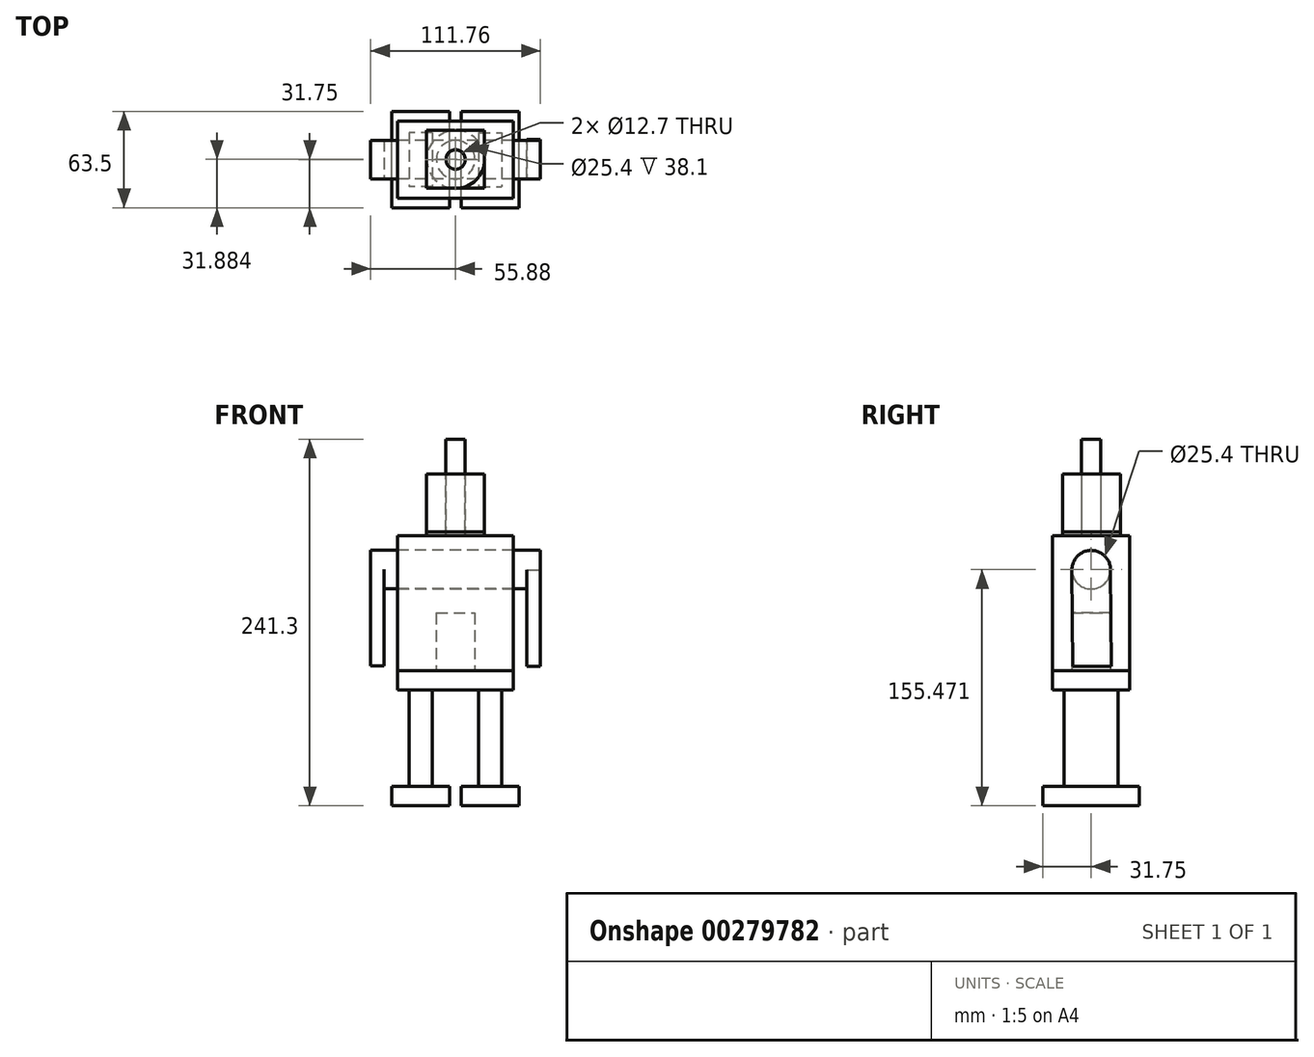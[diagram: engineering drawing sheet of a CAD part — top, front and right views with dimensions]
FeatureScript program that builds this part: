
annotation { "Feature Type Name" : "Feature", "Feature Type Description" : "" }
export const myFeature = defineFeature(function(context is Context, id is Id, definition is map)
    precondition{}
    {
        {
            var Q0;
            Q0=qCreatedBy(makeId("Front.planeOp"),FACE);
            var sketch = newSketch(context, id + "F0", { "sketchPlane" : qUnion([Q0])});
            skLineSegment(sketch, "E0.bottom", {"start": v(38.1, -57.15) * mm, "end": v(-38.1, -57.15) * mm});
            skLineSegment(sketch, "E0.top", {"start": v(38.1, 57.15) * mm, "end": v(-38.1, 57.15) * mm});
            skLineSegment(sketch, "E0.left", {"start": v(38.1, -57.15) * mm, "end": v(38.1, 57.15) * mm});
            skLineSegment(sketch, "E0.right", {"start": v(-38.1, -57.15) * mm, "end": v(-38.1, 57.15) * mm});
            skPoint(sketch, "E0.middle", {"position": v(0, 0) * mm});
            skSolve(sketch);
        }
        {
            var Q0;
            Q0 = qSketchRegion(id + "F0", true);
            extrude(context, id + "F1", {"entities" : qUnion([Q0]), "depth" : 50.8 * mm});
        }
        {
            var Q0;
            Q0=makeQuery(id+"F1.opExtrude","SWEPT_FACE",FACE,{"disambiguationData":[OSD([sQuery(id+"F0.wireOp",EDGE,"E0.left")])]});
            var sketch = newSketch(context, id + "F2", { "sketchPlane" : qUnion([Q0])});
            skCircle(sketch, "E1", {"center": v(-25.4, 34.82) * mm, "radius": 12.7 * mm});
            skPoint(sketch, "E1.centerSnap0", {"position": v(-25.4, 57.15) * mm});
            skSolve(sketch);
        }
        {
            var Q0;
            Q0 = qSketchRegion(id + "F2", true);
            extrude(context, id + "F3", {"entities" : qUnion([Q0]), "operationType" : NewBodyOperationType.REMOVE, "oppositeDirection" : true, "depth" : 76.2 * mm});
        }
        {
            var Q0;
            Q0=makeQuery(id+"F1.opExtrude","SWEPT_FACE",FACE,{"disambiguationData":[OSD([sQuery(id+"F0.wireOp",EDGE,"E0.bottom")])]});
            var sketch = newSketch(context, id + "F4", { "sketchPlane" : qUnion([Q0])});
            skCircle(sketch, "E2", {"center": v(0, 25.4) * mm, "radius": 12.7 * mm});
            skPoint(sketch, "E2.centerSnap0", {"position": v(-38.1, 25.4) * mm});
            skSolve(sketch);
        }
        {
            var Q0;
            Q0 = qSketchRegion(id + "F4", true);
            var Q1;
            Q1=makeQuery(id+"F4.imprint","IMPRINT",FACE,{"disambiguationData":[TD([[makeQuery(id+"F4.imprint","IMPRINT",EDGE,{"derivedFrom":sQuery(id+"F4.wireOp",EDGE,"E2")}),-1.0]])]});
            extrude(context, id + "F5", {"entities" : qUnion([Q0, Q1]), "operationType" : NewBodyOperationType.REMOVE, "oppositeDirection" : true, "depth" : 25.4 * mm});
        }
        {
            var Q0;
            Q0=makeQuery(id+"F5.boolean.opBoolean","COPY",FACE,{"derivedFrom":makeQuery(id+"F5.opExtrude","CAP_FACE",FACE,{"disambiguationData":[OSD([sQuery(id+"F0.wireOp",EDGE,"E0.bottom"),sQuery(id+"F0.wireOp",EDGE,"E0.left"),sQuery(id+"F0.wireOp",EDGE,"E0.right")])],"isStart":false})});
            var sketch = newSketch(context, id + "F6", { "sketchPlane" : qUnion([Q0])});
            skCircle(sketch, "E3", {"center": v(0, 25.4) * mm, "radius": 12.7 * mm});
            skPoint(sketch, "E3.centerSnap0", {"position": v(-38.1, 25.4) * mm});
            skSolve(sketch);
        }
        {
            var Q0;
            Q0=makeQuery(id+"F6.imprint","IMPRINT",FACE,{"disambiguationData":[TD([[makeQuery(id+"F6.imprint","IMPRINT",EDGE,{"derivedFrom":sQuery(id+"F6.wireOp",EDGE,"E3")}),1.0]])]});
            extrude(context, id + "F7", {"entities" : qUnion([Q0]), "operationType" : NewBodyOperationType.REMOVE, "oppositeDirection" : true, "depth" : 38.1 * mm});
        }
        {
            var Q0;
            Q0=makeQuery(id+"F1.opExtrude","SWEPT_FACE",FACE,{"disambiguationData":[OSD([sQuery(id+"F0.wireOp",EDGE,"E0.left")])]});
            var sketch = newSketch(context, id + "F8", { "sketchPlane" : qUnion([Q0])});
            skCircle(sketch, "E4", {"center": v(-25.4, 34.82) * mm, "radius": 12.7 * mm});
            skSolve(sketch);
        }
        {
            var Q0;
            Q0 = qSketchRegion(id + "F8", true);
            extrude(context, id + "F9", {"entities" : qUnion([Q0]), "depth" : 17.78 * mm, "hasSecondDirection" : true, "secondDirectionOppositeDirection" : true, "secondDirectionDepth" : 93.98 * mm});
        }
        {
            var Q0;
            Q0=makeQuery(id+"F9.opExtrude","CAP_FACE",FACE,{"disambiguationData":[OSD([sQuery(id+"F8.wireOp",EDGE,"E4")])],"isStart":false});
            var sketch = newSketch(context, id + "F10", { "sketchPlane" : qUnion([Q0])});
            skLineSegment(sketch, "E5", {"start": v(-38.1, 34.7) * mm, "end": v(-37.46, -28.8) * mm});
            skLineSegment(sketch, "E6", {"start": v(-12.7, 34.56) * mm, "end": v(-12.07, -28.94) * mm});
            skLineSegment(sketch, "E7", {"start": v(-12.07, -28.94) * mm, "end": v(-37.46, -28.8) * mm});
            skSolve(sketch);
        }
        {
            var Q0;
            Q0 = qSketchRegion(id + "F10", true);
            var Q1;
            {var subQ0=sQuery(id+"F10.wireOp",EDGE,"E5");Q1=makeQuery(id+"F10.imprint","IMPRINT",FACE,{"disambiguationData":[TD([[makeQuery(id+"F10.imprint","IMPRINT",EDGE,{"derivedFrom":subQ0}),1.0]])]});}
            extrude(context, id + "F11", {"entities" : qUnion([Q0, Q1]), "operationType" : NewBodyOperationType.ADD, "oppositeDirection" : true, "depth" : 8.9 * mm});
        }
        {
            var Q0;
            Q0=makeQuery(id+"F9.opExtrude","CAP_FACE",FACE,{"disambiguationData":[OSD([sQuery(id+"F8.wireOp",EDGE,"E4")])],"isStart":true});
            var sketch = newSketch(context, id + "F12", { "sketchPlane" : qUnion([Q0])});
            skLineSegment(sketch, "E8.bottom", {"start": v(12.7, 34.84) * mm, "end": v(38.1, 34.84) * mm});
            skLineSegment(sketch, "E8.top", {"start": v(12.7, -28.66) * mm, "end": v(38.1, -28.66) * mm});
            skLineSegment(sketch, "E8.left", {"start": v(12.7, 34.84) * mm, "end": v(12.7, -28.66) * mm});
            skLineSegment(sketch, "E8.right", {"start": v(38.1, 34.84) * mm, "end": v(38.1, -28.66) * mm});
            skSolve(sketch);
        }
        {
            var Q0;
            Q0 = qSketchRegion(id + "F12", true);
            extrude(context, id + "F13", {"entities" : qUnion([Q0]), "operationType" : NewBodyOperationType.ADD, "oppositeDirection" : true, "depth" : 8.9 * mm});
        }
        {
            var Q0;
            Q0=makeQuery(id+"F5.boolean.opBoolean","COPY",FACE,{"derivedFrom":makeQuery(id+"F5.opExtrude","CAP_FACE",FACE,{"disambiguationData":[OSD([sQuery(id+"F0.wireOp",EDGE,"E0.bottom"),sQuery(id+"F0.wireOp",EDGE,"E0.left"),sQuery(id+"F0.wireOp",EDGE,"E0.right")])],"isStart":false})});
            var sketch = newSketch(context, id + "F14", { "sketchPlane" : qUnion([Q0])});
            skLineSegment(sketch, "E9.bottom", {"start": v(38.1, 0) * mm, "end": v(-38.1, 0) * mm});
            skLineSegment(sketch, "E9.top", {"start": v(38.1, 50.8) * mm, "end": v(-38.1, 50.8) * mm});
            skLineSegment(sketch, "E9.left", {"start": v(38.1, 0) * mm, "end": v(38.1, 50.8) * mm});
            skLineSegment(sketch, "E9.right", {"start": v(-38.1, 0) * mm, "end": v(-38.1, 50.8) * mm});
            skPoint(sketch, "E9.middle", {"position": v(0, 25.4) * mm});
            skSolve(sketch);
        }
        {
            var Q0;
            Q0 = qSketchRegion(id + "F14", true);
            extrude(context, id + "F15", {"entities" : qUnion([Q0]), "depth" : 12.7 * mm});
        }
        {
            var Q0;
            Q0=makeQuery(id+"F15.opExtrude","CAP_FACE",FACE,{"disambiguationData":[OSD([sQuery(id+"F14.wireOp",EDGE,"E9.bottom"),sQuery(id+"F14.wireOp",EDGE,"E9.top"),sQuery(id+"F14.wireOp",EDGE,"E9.left"),sQuery(id+"F14.wireOp",EDGE,"E9.right")])],"isStart":false});
            var sketch = newSketch(context, id + "F16", { "sketchPlane" : qUnion([Q0])});
            skLineSegment(sketch, "E10.bottom", {"start": v(-15.24, 7.62) * mm, "end": v(-30.48, 7.62) * mm});
            skLineSegment(sketch, "E10.top", {"start": v(-15.24, 43.18) * mm, "end": v(-30.48, 43.18) * mm});
            skLineSegment(sketch, "E10.left", {"start": v(-15.24, 7.62) * mm, "end": v(-15.24, 43.18) * mm});
            skLineSegment(sketch, "E10.right", {"start": v(-30.48, 7.62) * mm, "end": v(-30.48, 43.18) * mm});
            skPoint(sketch, "E10.middle", {"position": v(-22.86, 25.4) * mm});
            skPoint(sketch, "E10.middle.positionSnap0", {"position": v(-38.1, 25.4) * mm});
            skPoint(sketch, "E10.centerSnap0", {"position": v(-38.1, 25.4) * mm});
            skLineSegment(sketch, "E11.MirrorCS", {"start": v(15.24, 43.18) * mm, "end": v(30.48, 43.18) * mm});
            skLineSegment(sketch, "E12.MirrorCS", {"start": v(30.48, 7.62) * mm, "end": v(30.48, 43.18) * mm});
            skLineSegment(sketch, "E13.MirrorCS", {"start": v(15.24, 7.62) * mm, "end": v(15.24, 43.18) * mm});
            skLineSegment(sketch, "E14.MirrorCS", {"start": v(15.24, 7.62) * mm, "end": v(30.48, 7.62) * mm});
            skPoint(sketch, "E15.MirrorP", {"position": v(22.86, 25.4) * mm});
            skSolve(sketch);
        }
        {
            var Q0;
            Q0=makeQuery(id+"F16.imprint","IMPRINT",FACE,{"disambiguationData":[TD([[makeQuery(id+"F16.imprint","IMPRINT",EDGE,{"derivedFrom":sQuery(id+"F16.wireOp",EDGE,"E10.bottom")}),-1.0]])]});
            var Q1;
            Q1=makeQuery(id+"F16.imprint","IMPRINT",FACE,{"disambiguationData":[TD([[makeQuery(id+"F16.imprint","IMPRINT",EDGE,{"derivedFrom":sQuery(id+"F16.wireOp",EDGE,"E11.MirrorCS")}),-1.0]])]});
            extrude(context, id + "F17", {"entities" : qUnion([Q0, Q1]), "depth" : 63.5 * mm});
        }
        {
            var Q0;
            Q0=makeQuery(id+"F17.opExtrude","CAP_FACE",FACE,{"disambiguationData":[OSD([sQuery(id+"F16.wireOp",EDGE,"E10.bottom"),sQuery(id+"F16.wireOp",EDGE,"E10.top"),sQuery(id+"F16.wireOp",EDGE,"E10.left"),sQuery(id+"F16.wireOp",EDGE,"E10.right")])],"isStart":false});
            var sketch = newSketch(context, id + "F18", { "sketchPlane" : qUnion([Q0])});
            skLineSegment(sketch, "E16.bottom", {"start": v(-3.81, 57.15) * mm, "end": v(-41.91, 57.15) * mm});
            skLineSegment(sketch, "E16.top", {"start": v(-3.81, -6.35) * mm, "end": v(-41.91, -6.35) * mm});
            skLineSegment(sketch, "E16.left", {"start": v(-3.81, 57.15) * mm, "end": v(-3.81, -6.35) * mm});
            skLineSegment(sketch, "E16.right", {"start": v(-41.91, 57.15) * mm, "end": v(-41.91, -6.35) * mm});
            skPoint(sketch, "E16.middle", {"position": v(-22.86, 25.4) * mm});
            skPoint(sketch, "E16.middle.positionSnap0", {"position": v(-30.48, 25.4) * mm});
            skPoint(sketch, "E16.middle.positionSnap1", {"position": v(-22.86, 7.62) * mm});
            skPoint(sketch, "E16.centerSnap0", {"position": v(-30.48, 25.4) * mm});
            skPoint(sketch, "E16.centerSnap1", {"position": v(-22.86, 7.62) * mm});
            skLineSegment(sketch, "E17.MirrorCS", {"start": v(3.8, 57.15) * mm, "end": v(3.8, -6.35) * mm});
            skLineSegment(sketch, "E18.MirrorCS", {"start": v(3.8, 57.15) * mm, "end": v(41.9, 57.15) * mm});
            skLineSegment(sketch, "E19.MirrorCS", {"start": v(41.9, 57.15) * mm, "end": v(41.9, -6.35) * mm});
            skLineSegment(sketch, "E20.MirrorCS", {"start": v(3.8, -6.35) * mm, "end": v(41.91, -6.35) * mm});
            skSolve(sketch);
        }
        {
            var Q0;
            Q0=makeQuery(id+"F18.imprint","IMPRINT",FACE,{"disambiguationData":[TD([[makeQuery(id+"F18.imprint","IMPRINT",EDGE,{"derivedFrom":sQuery(id+"F18.wireOp",EDGE,"E16.bottom")}),1.0]])]});
            var Q1;
            Q1=makeQuery(id+"F18.imprint","IMPRINT",FACE,{"disambiguationData":[TD([[makeQuery(id+"F18.imprint","IMPRINT",EDGE,{"derivedFrom":sQuery(id+"F18.wireOp",EDGE,"E17.MirrorCS")}),1.0]])]});
            var Q2;
            Q2=makeQuery(id+"F18.imprint","IMPRINT",FACE,{"disambiguationData":[TD([[makeQuery(id+"F18.imprint","IMPRINT",EDGE,{"derivedFrom":makeQuery(id+"F17.opExtrude","CAP_EDGE",EDGE,{"disambiguationData":[OSD([sQuery(id+"F16.wireOp",EDGE,"E10.bottom")])],"isStart":false})}),-1.0]])]});
            extrude(context, id + "F19", {"entities" : qUnion([Q0, Q1, Q2]), "depth" : 12.7 * mm});
        }
        {
            var Q0;
            Q0=makeQuery(id+"F1.opExtrude","SWEPT_FACE",FACE,{"disambiguationData":[OSD([sQuery(id+"F0.wireOp",EDGE,"E0.top")])]});
            var sketch = newSketch(context, id + "F20", { "sketchPlane" : qUnion([Q0])});
            skCircle(sketch, "E21", {"center": v(0, -25.27) * mm, "radius": 19.05 * mm});
            skSolve(sketch);
        }
        {
            var Q0;
            Q0 = qSketchRegion(id + "F20", true);
            extrude(context, id + "F21", {"entities" : qUnion([Q0]), "depth" : 2.54 * mm});
        }
        {
            var Q0;
            Q0=makeQuery(id+"F21.opExtrude","CAP_FACE",FACE,{"disambiguationData":[OSD([sQuery(id+"F20.wireOp",EDGE,"E21")])],"isStart":false});
            var sketch = newSketch(context, id + "F22", { "sketchPlane" : qUnion([Q0])});
            skLineSegment(sketch, "E22.bottom", {"start": v(19.05, -44.32) * mm, "end": v(-19.05, -44.32) * mm});
            skLineSegment(sketch, "E22.top", {"start": v(19.05, -6.22) * mm, "end": v(-19.05, -6.22) * mm});
            skLineSegment(sketch, "E22.left", {"start": v(19.05, -44.32) * mm, "end": v(19.05, -6.22) * mm});
            skLineSegment(sketch, "E22.right", {"start": v(-19.05, -44.32) * mm, "end": v(-19.05, -6.22) * mm});
            skPoint(sketch, "E22.middle", {"position": v(0, -25.27) * mm});
            skSolve(sketch);
        }
        {
            var Q0;
            Q0 = qSketchRegion(id + "F22", true);
            extrude(context, id + "F23", {"entities" : qUnion([Q0]), "depth" : 38.1 * mm});
        }
        {
            var Q0;
            Q0=makeQuery(id+"F23.opExtrude","CAP_FACE",FACE,{"disambiguationData":[OSD([sQuery(id+"F22.wireOp",EDGE,"E22.bottom"),sQuery(id+"F22.wireOp",EDGE,"E22.top"),sQuery(id+"F22.wireOp",EDGE,"E22.left"),sQuery(id+"F22.wireOp",EDGE,"E22.right")])],"isStart":false});
            var sketch = newSketch(context, id + "F24", { "sketchPlane" : qUnion([Q0])});
            skCircle(sketch, "E23", {"center": v(0, -25.27) * mm, "radius": 6.35 * mm});
            skPoint(sketch, "E23.centerSnap0", {"position": v(-19.05, -25.27) * mm});
            skSolve(sketch);
        }
        {
            var Q0;
            Q0 = qSketchRegion(id + "F24", true);
            extrude(context, id + "F25", {"entities" : qUnion([Q0]), "operationType" : NewBodyOperationType.REMOVE, "oppositeDirection" : true, "depth" : 40.64 * mm});
        }
        {
            var Q0;
            Q0=makeQuery(id+"F1.opExtrude","SWEPT_FACE",FACE,{"disambiguationData":[OSD([sQuery(id+"F0.wireOp",EDGE,"E0.top")])]});
            var sketch = newSketch(context, id + "F26", { "sketchPlane" : qUnion([Q0])});
            skCircle(sketch, "E24", {"center": v(0, -25.4) * mm, "radius": 6.35 * mm});
            skPoint(sketch, "E24.centerSnap0", {"position": v(-38.1, -25.4) * mm});
            skSolve(sketch);
        }
        {
            var Q0;
            Q0 = qSketchRegion(id + "F26", true);
            extrude(context, id + "F27", {"entities" : qUnion([Q0]), "depth" : 63.5 * mm});
        }
        {
            var Q0;
            Q0=makeQuery(id+"F15.opExtrude","CAP_FACE",FACE,{"disambiguationData":[OSD([sQuery(id+"F14.wireOp",EDGE,"E9.bottom"),sQuery(id+"F14.wireOp",EDGE,"E9.top"),sQuery(id+"F14.wireOp",EDGE,"E9.left"),sQuery(id+"F14.wireOp",EDGE,"E9.right")])],"isStart":true});
            var sketch = newSketch(context, id + "F28", { "sketchPlane" : qUnion([Q0])});
            skCircle(sketch, "E25", {"center": v(0, -25.4) * mm, "radius": 12.7 * mm});
            skPoint(sketch, "E25.centerSnap0", {"position": v(-38.1, -25.4) * mm});
            skSolve(sketch);
        }
        {
            var Q0;
            Q0 = qSketchRegion(id + "F28", true);
            extrude(context, id + "F29", {"entities" : qUnion([Q0]), "depth" : 38.1 * mm});
        }
        {
            var Q0;
            Q0=makeQuery(id+"F21.opExtrude","CAP_FACE",FACE,{"disambiguationData":[OSD([sQuery(id+"F20.wireOp",EDGE,"E21")])],"isStart":false});
            var sketch = newSketch(context, id + "F30", { "sketchPlane" : qUnion([Q0])});
            skCircle(sketch, "E26", {"center": v(0, -25.27) * mm, "radius": 6.35 * mm});
            skSolve(sketch);
        }
        {
            var Q0;
            Q0=makeQuery(id+"F30.imprint","IMPRINT",FACE,{"disambiguationData":[TD([[makeQuery(id+"F30.imprint","IMPRINT",EDGE,{"derivedFrom":sQuery(id+"F30.wireOp",EDGE,"E26")}),1.0]])]});
            extrude(context, id + "F31", {"entities" : qUnion([Q0]), "operationType" : NewBodyOperationType.REMOVE, "oppositeDirection" : true, "depth" : 2.54 * mm});
        }
    });
